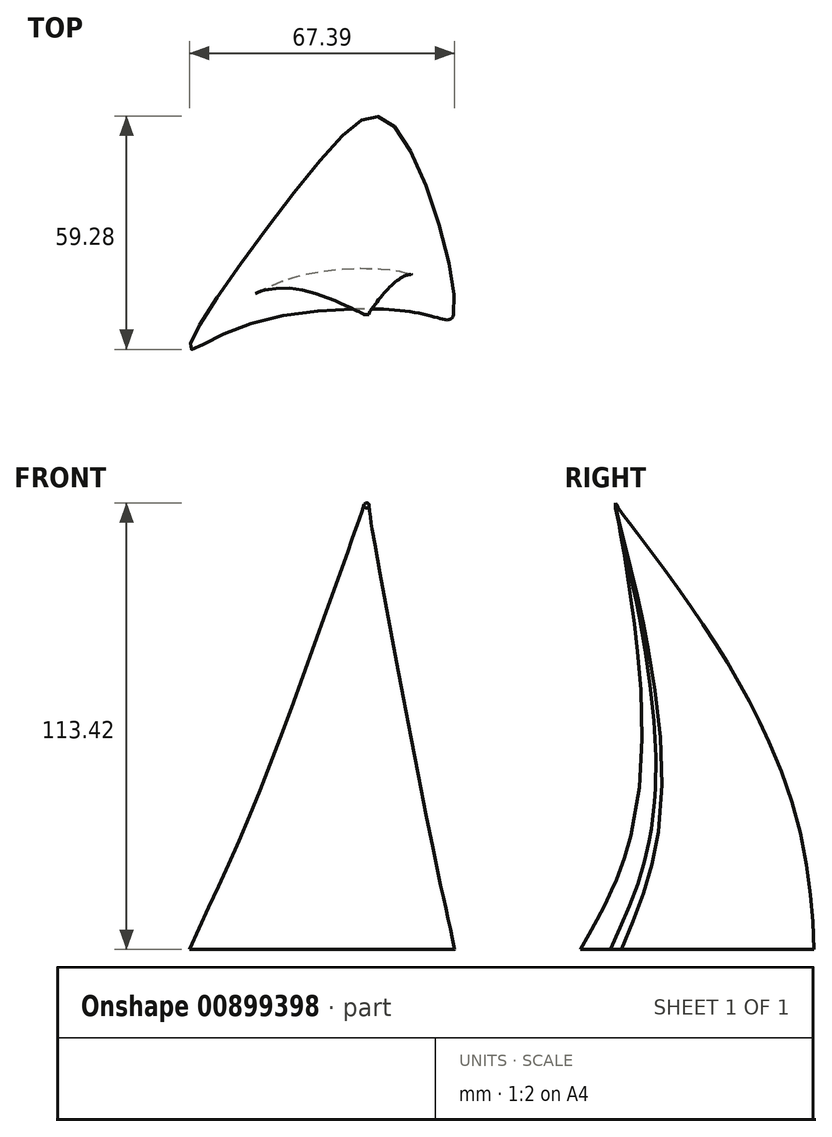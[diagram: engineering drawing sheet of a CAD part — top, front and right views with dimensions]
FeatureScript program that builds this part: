
annotation { "Feature Type Name" : "Feature", "Feature Type Description" : "" }
export const myFeature = defineFeature(function(context is Context, id is Id, definition is map)
    precondition{}
    {
        {
            var Q0;
            Q0=qCreatedBy(makeId("Top.planeOp"),FACE);
            var sketch = newSketch(context, id + "F0", { "sketchPlane" : qUnion([Q0])});
            skFitSpline(sketch, "E0", {"points": [v(0, 0) * mm, v(-15.4, 48.2) * mm, v(-33.05, 40.19) * mm, v(-67.12, -8.4) * mm, v(-53.81, -3.02) * mm, v(-6.98, 0) * mm, v(0, 0) * mm]});
            skSolve(sketch);
        }
        {
            var Q0;
            Q0=qCreatedBy(makeId("Right.planeOp"),FACE);
            var sketch = newSketch(context, id + "F1", { "sketchPlane" : qUnion([Q0])});
            skFitSpline(sketch, "E1", {"points": [v(25.73, 0) * mm, v(0, 83.67) * mm], "startDerivative": vector(3.86, 69.86) * mm, "endDerivative": vector(-72.72, 121.2) * mm});
            skSolve(sketch);
        }
        {
            var Q0;
            Q0=qCreatedBy(makeId("Front.planeOp"),FACE);
            var sketch = newSketch(context, id + "F2", { "sketchPlane" : qUnion([Q0])});
            skCircle(sketch, "E2", {"center": v(-22.1, 112.79) * mm, "radius": 0.64 * mm});
            skSolve(sketch);
        }
        {
            var Q0;
            Q0 = qConstructionFilter(qBodyType(qCreatedBy(id + "F1" ,EDGE), BodyType.WIRE), ConstructionObject.NO);
            var Q1;
            Q1 = qSketchRegion(id + "F0", true);
            var Q2;
            Q2 = qSketchRegion(id + "F2", true);
            loft(context, id + "F3", {"addSections" : true, "spine" : qUnion([Q0]), "sectionCount" : 5, "sheetProfilesArray" : [{ "sheetProfileEntities" : qUnion([Q1]) }, { "sheetProfileEntities" : qUnion([Q2]) }]});
        }
    });
